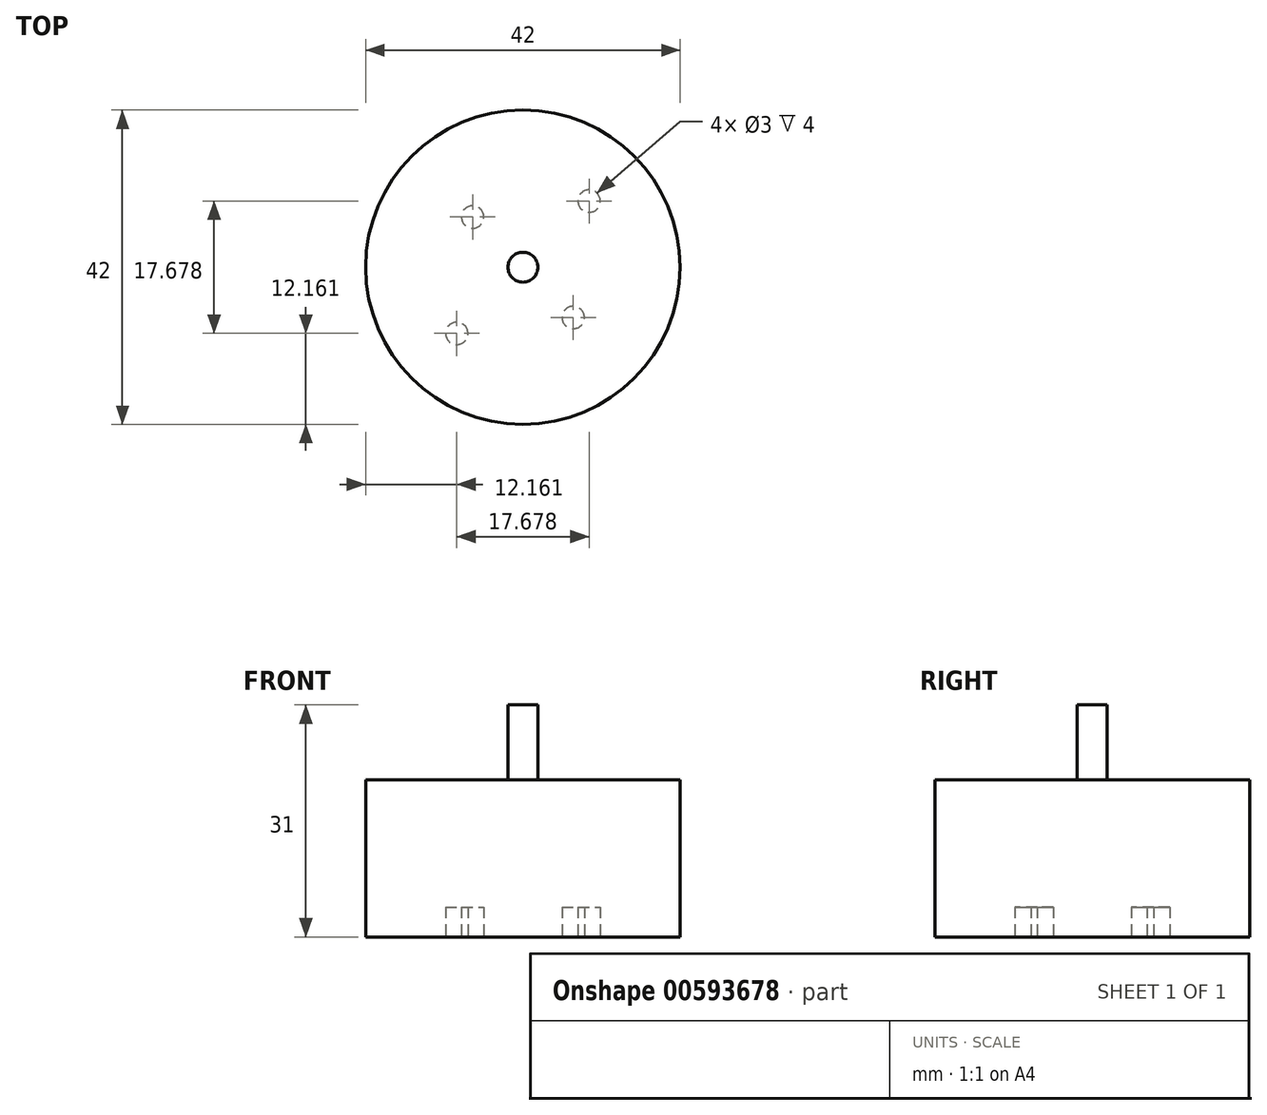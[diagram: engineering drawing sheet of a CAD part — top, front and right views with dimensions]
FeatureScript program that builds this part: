
annotation { "Feature Type Name" : "Feature", "Feature Type Description" : "" }
export const myFeature = defineFeature(function(context is Context, id is Id, definition is map)
    precondition{}
    {
        {
            var Q0;
            Q0=qCreatedBy(makeId("Front.planeOp"),FACE);
            var sketch = newSketch(context, id + "F0", { "sketchPlane" : qUnion([Q0])});
            skLineSegment(sketch, "E0", {"start": v(0, 0) * mm, "end": v(21, 0) * mm});
            skLineSegment(sketch, "E1", {"start": v(21, 0) * mm, "end": v(21, 21) * mm});
            skLineSegment(sketch, "E2", {"start": v(21, 21) * mm, "end": v(2, 21) * mm});
            skLineSegment(sketch, "E3", {"start": v(2, 21) * mm, "end": v(2, 31) * mm});
            skLineSegment(sketch, "E4", {"start": v(2, 31) * mm, "end": v(0, 31) * mm});
            skLineSegment(sketch, "E5", {"start": v(0, 31) * mm, "end": v(0, 0) * mm});
            skSolve(sketch);
        }
        {
            var Q0;
            Q0 = qSketchRegion(id + "F0", true);
            var Q1;
            Q1=sQuery(id+"F0.wireOp",EDGE,"E5");
            revolve(context, id + "F1", {"entities" : qUnion([Q0]), "axis" : qUnion([Q1]), "revolveType" : RevolveType.FULL});
        }
        {
            var Q0;
            Q0=makeQuery(id+"F1.opRevolve","SWEPT_FACE",FACE,{"disambiguationData":[OSD([sQuery(id+"F0.wireOp",EDGE,"E0")])]});
            var sketch = newSketch(context, id + "F2", { "sketchPlane" : qUnion([Q0])});
            skLineSegment(sketch, "E6", {"start": v(-6.72, -6.72) * mm, "end": v(6.72, 6.72) * mm, "construction": true});
            skLineSegment(sketch, "E7", {"start": v(8.84, -8.84) * mm, "end": v(-8.84, 8.84) * mm, "construction": true});
            skCircle(sketch, "E8", {"center": v(-6.72, -6.72) * mm, "radius": 1.5 * mm});
            skCircle(sketch, "E9", {"center": v(-8.84, 8.84) * mm, "radius": 1.5 * mm});
            skCircle(sketch, "E10", {"center": v(6.72, 6.72) * mm, "radius": 1.5 * mm});
            skCircle(sketch, "E11", {"center": v(8.84, -8.84) * mm, "radius": 1.5 * mm});
            skSolve(sketch);
        }
        {
            var Q0;
            Q0 = qSketchRegion(id + "F2", true);
            extrude(context, id + "F3", {"entities" : qUnion([Q0]), "operationType" : NewBodyOperationType.REMOVE, "oppositeDirection" : true, "depth" : 4 * mm, "offsetDistance" : 25 * mm});
        }
    });
